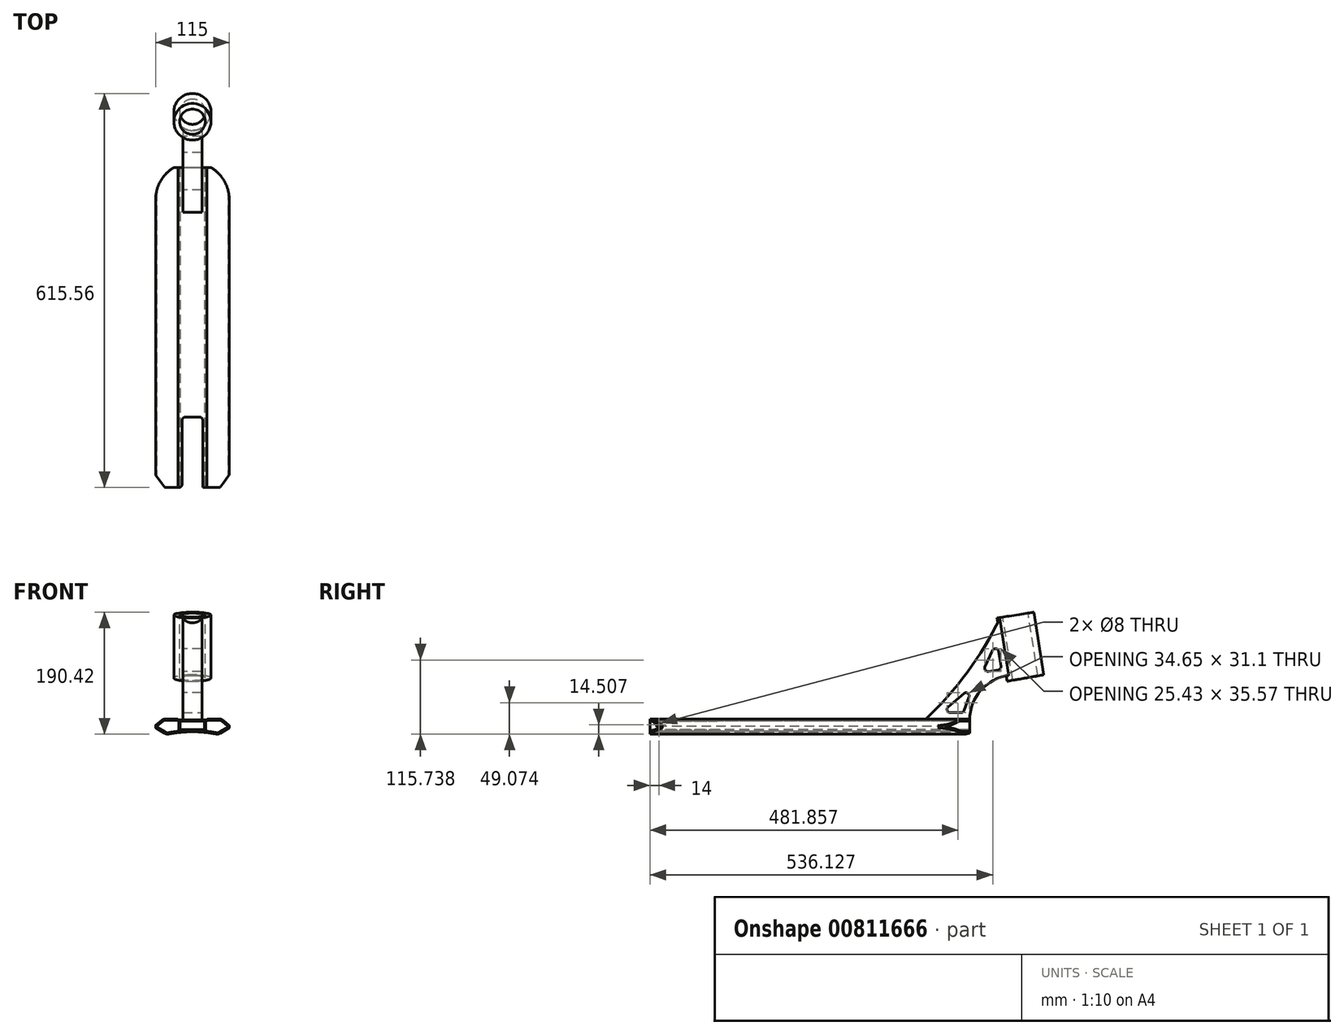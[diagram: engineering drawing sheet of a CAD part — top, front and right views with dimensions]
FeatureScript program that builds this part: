
annotation { "Feature Type Name" : "Feature", "Feature Type Description" : "" }
export const myFeature = defineFeature(function(context is Context, id is Id, definition is map)
    precondition{}
    {
        {
            var Q0;
            Q0=qCreatedBy(makeId("Front.planeOp"),FACE);
            var sketch = newSketch(context, id + "F0", { "sketchPlane" : qUnion([Q0])});
            skLineSegment(sketch, "E0", {"start": v(0, 46.76) * mm, "end": v(0, 0) * mm, "construction": true});
            skLineSegment(sketch, "E1", {"start": v(22.5, 13.36) * mm, "end": v(45.58, 13.36) * mm});
            skLineSegment(sketch, "E2", {"start": v(45.58, 13.36) * mm, "end": v(57.5, 3.36) * mm});
            skLineSegment(sketch, "E3", {"start": v(57.5, 3.36) * mm, "end": v(57.5, -0.64) * mm});
            skLineSegment(sketch, "E4", {"start": v(57.5, -0.64) * mm, "end": v(40.18, -10.64) * mm});
            skLineSegment(sketch, "E5.MirrorCS", {"start": v(-22.5, 13.36) * mm, "end": v(-45.58, 13.36) * mm});
            skLineSegment(sketch, "E6.MirrorCS", {"start": v(-45.58, 13.36) * mm, "end": v(-57.5, 3.36) * mm});
            skLineSegment(sketch, "E7.MirrorCS", {"start": v(-57.5, -0.64) * mm, "end": v(-40.18, -10.64) * mm});
            skLineSegment(sketch, "E8.MirrorCS", {"start": v(-57.5, 3.36) * mm, "end": v(-57.5, -0.64) * mm});
            skArc(sketch, "E9", {"start": v(40.18, -10.64) * mm, "mid": v(0, -6.56) * mm, "end": v(-40.18, -10.64) * mm});
            skLineSegment(sketch, "E10", {"start": v(-22.5, 13.36) * mm, "end": v(-22.5, 12.06) * mm});
            skLineSegment(sketch, "E11", {"start": v(-22.5, 12.06) * mm, "end": v(22.5, 12.06) * mm});
            skLineSegment(sketch, "E12", {"start": v(22.5, 12.06) * mm, "end": v(22.5, 13.36) * mm});
            skSolve(sketch);
        }
        {
            var Q0;
            Q0 = qSketchRegion(id + "F0", true);
            extrude(context, id + "F1", {"entities" : qUnion([Q0]), "endBound" : BoundingType.SYMMETRIC, "depth" : 500 * mm, "offsetDistance" : 25 * mm});
        }
        {
            var Q0;
            Q0=qCreatedBy(makeId("Front.planeOp"),FACE);
            var sketch = newSketch(context, id + "F2", { "sketchPlane" : qUnion([Q0])});
            skLineSegment(sketch, "E13.bottom", {"start": v(-19, 10.06) * mm, "end": v(19, 10.06) * mm});
            skLineSegment(sketch, "E13.top", {"start": v(-19, -2.94) * mm, "end": v(19, -2.94) * mm});
            skLineSegment(sketch, "E13.left", {"start": v(-19, 10.06) * mm, "end": v(-19, -2.94) * mm});
            skLineSegment(sketch, "E13.right", {"start": v(19, 10.06) * mm, "end": v(19, -2.94) * mm});
            skSolve(sketch);
        }
        {
            var Q0;
            Q0 = qSketchRegion(id + "F2", true);
            extrude(context, id + "F3", {"entities" : qUnion([Q0]), "operationType" : NewBodyOperationType.REMOVE, "endBound" : BoundingType.SYMMETRIC, "oppositeDirection" : true, "depth" : 500 * mm, "offsetDistance" : 25 * mm});
        }
        {
            var Q0;
            Q0=makeQuery(id+"F1.opExtrude","SWEPT_EDGE",EDGE,{"disambiguationData":[OSD([sQuery(id+"F0.wireOp",EDGE,"E1"),sQuery(id+"F0.wireOp",EDGE,"E12")])]});
            var Q1;
            Q1=makeQuery(id+"F1.opExtrude","SWEPT_EDGE",EDGE,{"disambiguationData":[OSD([sQuery(id+"F0.wireOp",EDGE,"E5.MirrorCS"),sQuery(id+"F0.wireOp",EDGE,"E10")])]});
            fillet(context, id + "F4", {"entities" : qUnion([Q0, Q1]), "radius" : 2 * mm, "tangentPropagation" : true, "allowEdgeOverflow" : false});
        }
        {
            var Q0;
            Q0=makeQuery(id+"F1.opExtrude","SWEPT_EDGE",EDGE,{"disambiguationData":[OSD([sQuery(id+"F0.wireOp",EDGE,"E5.MirrorCS"),sQuery(id+"F0.wireOp",EDGE,"E6.MirrorCS")])]});
            var Q1;
            Q1=makeQuery(id+"F1.opExtrude","SWEPT_EDGE",EDGE,{"disambiguationData":[OSD([sQuery(id+"F0.wireOp",EDGE,"E7.MirrorCS"),sQuery(id+"F0.wireOp",EDGE,"E9")])]});
            var Q2;
            Q2=makeQuery(id+"F1.opExtrude","SWEPT_EDGE",EDGE,{"disambiguationData":[OSD([sQuery(id+"F0.wireOp",EDGE,"E4"),sQuery(id+"F0.wireOp",EDGE,"E9")])]});
            var Q3;
            Q3=makeQuery(id+"F1.opExtrude","SWEPT_EDGE",EDGE,{"disambiguationData":[OSD([sQuery(id+"F0.wireOp",EDGE,"E1"),sQuery(id+"F0.wireOp",EDGE,"E2")])]});
            fillet(context, id + "F5", {"entities" : qUnion([Q0, Q1, Q2, Q3]), "radius" : 9 * mm, "tangentPropagation" : true, "allowEdgeOverflow" : false});
        }
        {
            var Q0;
            Q0=makeQuery(id+"F1.opExtrude","SWEPT_EDGE",EDGE,{"disambiguationData":[OSD([sQuery(id+"F0.wireOp",EDGE,"E2"),sQuery(id+"F0.wireOp",EDGE,"E3")])]});
            var Q1;
            Q1=makeQuery(id+"F1.opExtrude","SWEPT_EDGE",EDGE,{"disambiguationData":[OSD([sQuery(id+"F0.wireOp",EDGE,"E3"),sQuery(id+"F0.wireOp",EDGE,"E4")])]});
            var Q2;
            Q2=makeQuery(id+"F1.opExtrude","SWEPT_EDGE",EDGE,{"disambiguationData":[OSD([sQuery(id+"F0.wireOp",EDGE,"E7.MirrorCS"),sQuery(id+"F0.wireOp",EDGE,"E8.MirrorCS")])]});
            var Q3;
            Q3=makeQuery(id+"F1.opExtrude","SWEPT_EDGE",EDGE,{"disambiguationData":[OSD([sQuery(id+"F0.wireOp",EDGE,"E6.MirrorCS"),sQuery(id+"F0.wireOp",EDGE,"E8.MirrorCS")])]});
            fillet(context, id + "F6", {"entities" : qUnion([Q0, Q1, Q2, Q3]), "radius" : 1 * mm, "tangentPropagation" : true, "allowEdgeOverflow" : false});
        }
        {
            var Q0;
            Q0=makeQuery(id+"F1.opExtrude","CAP_FACE",FACE,{"disambiguationData":[OSD([sQuery(id+"F0.wireOp",EDGE,"E1"),sQuery(id+"F0.wireOp",EDGE,"E2"),sQuery(id+"F0.wireOp",EDGE,"E3"),sQuery(id+"F0.wireOp",EDGE,"E4"),sQuery(id+"F0.wireOp",EDGE,"E5.MirrorCS"),sQuery(id+"F0.wireOp",EDGE,"E6.MirrorCS"),sQuery(id+"F0.wireOp",EDGE,"E7.MirrorCS"),sQuery(id+"F0.wireOp",EDGE,"E8.MirrorCS"),sQuery(id+"F0.wireOp",EDGE,"E9"),sQuery(id+"F0.wireOp",EDGE,"E10"),sQuery(id+"F0.wireOp",EDGE,"E11"),sQuery(id+"F0.wireOp",EDGE,"E12")])],"isStart":false});
            var sketch = newSketch(context, id + "F7", { "sketchPlane" : qUnion([Q0])});
            skLineSegment(sketch, "E14.0.0", {"start": v(-48.1, 11.26) * mm, "end": v(-57.14, 3.66) * mm});
            skArc(sketch, "E14.0.1", {"start": v(-57.14, 3.66) * mm, "mid": v(-57.4, 3.32) * mm, "end": v(-57.5, 2.9) * mm});
            skLineSegment(sketch, "E14.0.2", {"start": v(-57.5, 2.9) * mm, "end": v(-57.5, -0.06) * mm});
            skArc(sketch, "E14.0.3", {"start": v(-57.5, -0.06) * mm, "mid": v(-57.37, -0.56) * mm, "end": v(-57, -0.92) * mm});
            skLineSegment(sketch, "E14.0.4", {"start": v(-57, -0.92) * mm, "end": v(-43.1, -8.95) * mm});
            skArc(sketch, "E14.0.5", {"start": v(-43.1, -8.95) * mm, "mid": v(-40.12, -10.03) * mm, "end": v(-36.94, -10) * mm});
            skArc(sketch, "E14.0.6", {"start": v(-36.94, -10) * mm, "mid": v(0, -6.56) * mm, "end": v(36.94, -10) * mm});
            skArc(sketch, "E14.0.7", {"start": v(36.94, -10) * mm, "mid": v(40.12, -10.03) * mm, "end": v(43.1, -8.95) * mm});
            skLineSegment(sketch, "E14.0.8", {"start": v(43.1, -8.95) * mm, "end": v(57, -0.92) * mm});
            skArc(sketch, "E14.0.9", {"start": v(57, -0.92) * mm, "mid": v(57.37, -0.56) * mm, "end": v(57.5, -0.06) * mm});
            skLineSegment(sketch, "E14.0.10", {"start": v(57.5, -0.06) * mm, "end": v(57.5, 2.9) * mm});
            skArc(sketch, "E14.0.11", {"start": v(57.5, 2.9) * mm, "mid": v(57.4, 3.32) * mm, "end": v(57.14, 3.66) * mm});
            skLineSegment(sketch, "E14.0.12", {"start": v(57.14, 3.66) * mm, "end": v(48.1, 11.26) * mm});
            skArc(sketch, "E14.0.13", {"start": v(48.1, 11.26) * mm, "mid": v(45.38, 12.82) * mm, "end": v(42.3, 13.36) * mm});
            skLineSegment(sketch, "E14.0.14", {"start": v(42.3, 13.36) * mm, "end": v(24.37, 13.36) * mm});
            skArc(sketch, "E14.0.15", {"start": v(24.37, 13.36) * mm, "mid": v(23.23, 13) * mm, "end": v(22.5, 12.06) * mm});
            skLineSegment(sketch, "E14.0.16", {"start": v(22.5, 12.06) * mm, "end": v(-22.5, 12.06) * mm});
            skArc(sketch, "E14.0.17", {"start": v(-22.5, 12.06) * mm, "mid": v(-23.23, 13) * mm, "end": v(-24.37, 13.36) * mm});
            skLineSegment(sketch, "E14.0.18", {"start": v(-24.37, 13.36) * mm, "end": v(-42.3, 13.36) * mm});
            skArc(sketch, "E14.0.19", {"start": v(-42.3, 13.36) * mm, "mid": v(-45.38, 12.82) * mm, "end": v(-48.1, 11.26) * mm});
            skArc(sketch, "E15.0", {"start": v(-37.3, -8.03) * mm, "mid": v(0, -4.56) * mm, "end": v(37.3, -8.03) * mm});
            skArc(sketch, "E15.1", {"start": v(-42.1, -7.22) * mm, "mid": v(-39.78, -8.05) * mm, "end": v(-37.3, -8.03) * mm});
            skLineSegment(sketch, "E15.2", {"start": v(-55.62, 0.59) * mm, "end": v(-42.1, -7.22) * mm});
            skLineSegment(sketch, "E15.6", {"start": v(-24.37, 11.36) * mm, "end": v(-24.37, 11.36) * mm});
            skLineSegment(sketch, "E15.7", {"start": v(-24.37, 11.36) * mm, "end": v(-42.3, 11.36) * mm});
            skArc(sketch, "E15.8", {"start": v(-42.3, 11.36) * mm, "mid": v(-44.7, 10.94) * mm, "end": v(-46.8, 9.73) * mm});
            skLineSegment(sketch, "E15.9", {"start": v(-46.8, 9.73) * mm, "end": v(-55.86, 2.13) * mm});
            skArc(sketch, "E16", {"start": v(-55.86, 2.13) * mm, "mid": v(-56.1, 1.3) * mm, "end": v(-55.62, 0.59) * mm});
            skArc(sketch, "E17", {"start": v(-22.5, 10.06) * mm, "mid": v(-23.23, 11) * mm, "end": v(-24.37, 11.36) * mm});
            skLineSegment(sketch, "E18", {"start": v(-22.5, 10.06) * mm, "end": v(-21, 10.06) * mm});
            skLineSegment(sketch, "E19", {"start": v(-21, 10.06) * mm, "end": v(-21, -5.65) * mm});
            skLineSegment(sketch, "E20", {"start": v(0, 12.06) * mm, "end": v(0, 30.3) * mm, "construction": true});
            skLineSegment(sketch, "E21.MirrorCS", {"start": v(24.37, 11.36) * mm, "end": v(42.3, 11.36) * mm});
            skArc(sketch, "E22.MirrorCS", {"start": v(42.3, 11.36) * mm, "mid": v(44.7, 10.94) * mm, "end": v(46.8, 9.73) * mm});
            skLineSegment(sketch, "E23.MirrorCS", {"start": v(46.8, 9.73) * mm, "end": v(55.86, 2.13) * mm});
            skArc(sketch, "E24.MirrorCS", {"start": v(55.86, 2.13) * mm, "mid": v(56.1, 1.3) * mm, "end": v(55.62, 0.59) * mm});
            skLineSegment(sketch, "E25.MirrorCS", {"start": v(55.62, 0.59) * mm, "end": v(42.1, -7.22) * mm});
            skArc(sketch, "E26.MirrorCS", {"start": v(42.1, -7.22) * mm, "mid": v(39.78, -8.05) * mm, "end": v(37.3, -8.03) * mm});
            skArc(sketch, "E27.MirrorCS", {"start": v(37.3, -8.03) * mm, "mid": v(0, -4.56) * mm, "end": v(-37.3, -8.03) * mm});
            skLineSegment(sketch, "E28.MirrorCS", {"start": v(21, 10.06) * mm, "end": v(21, -5.65) * mm});
            skLineSegment(sketch, "E29.MirrorCS", {"start": v(22.5, 10.06) * mm, "end": v(21, 10.06) * mm});
            skArc(sketch, "E30.MirrorCS", {"start": v(22.5, 10.06) * mm, "mid": v(23.23, 11) * mm, "end": v(24.37, 11.36) * mm});
            skSolve(sketch);
        }
        {
            var Q0;
            Q0=makeQuery(id+"F7.imprint","IMPRINT",FACE,{"disambiguationData":[TD([[makeQuery(id+"F7.imprint","IMPRINT",EDGE,{"derivedFrom":makeQuery(id+"F3.boolean.opBoolean","COPY",EDGE,{"derivedFrom":makeQuery(id+"F3.opExtrude","CAP_EDGE",EDGE,{"disambiguationData":[OSD([sQuery(id+"F2.wireOp",EDGE,"E13.bottom")])],"isStart":true})})}),-1.0]])]});
            var Q1;
            {var subQ0=sQuery(id+"F7.wireOp",EDGE,"E15.1");Q1=makeQuery(id+"F7.imprint","IMPRINT",FACE,{"disambiguationData":[TD([[makeQuery(id+"F7.imprint","IMPRINT",EDGE,{"derivedFrom":subQ0}),1.0]])]});}
            var Q2;
            Q2=makeQuery(id+"F7.imprint","IMPRINT",FACE,{"disambiguationData":[TD([[makeQuery(id+"F7.imprint","IMPRINT",EDGE,{"derivedFrom":sQuery(id+"F7.wireOp",EDGE,"E21.MirrorCS")}),-1.0]])]});
            extrude(context, id + "F8", {"entities" : qUnion([Q0, Q1, Q2]), "operationType" : NewBodyOperationType.REMOVE, "endBound" : BoundingType.THROUGH_ALL, "oppositeDirection" : true, "depth" : 25 * mm, "offsetDistance" : 25 * mm});
        }
        {
            var Q0;
            Q0=qCreatedBy(makeId("Top.planeOp"),FACE);
            var sketch = newSketch(context, id + "F9", { "sketchPlane" : qUnion([Q0])});
            skArc(sketch, "E31", {"start": v(57.5, 200) * mm, "mid": v(0, 257.5) * mm, "end": v(-57.5, 200) * mm});
            skLineSegment(sketch, "E32", {"start": v(-57.5, 200) * mm, "end": v(-57.5, 280) * mm});
            skLineSegment(sketch, "E33", {"start": v(57.5, 200) * mm, "end": v(57.5, 280) * mm});
            skLineSegment(sketch, "E34", {"start": v(57.5, 280) * mm, "end": v(-57.5, 280) * mm});
            skSolve(sketch);
        }
        {
            var Q0;
            Q0 = qSketchRegion(id + "F9", true);
            extrude(context, id + "F10", {"entities" : qUnion([Q0]), "operationType" : NewBodyOperationType.REMOVE, "endBound" : BoundingType.THROUGH_ALL, "oppositeDirection" : true, "depth" : 25 * mm, "offsetDistance" : 25 * mm, "hasSecondDirection" : true, "secondDirectionBound" : SecondDirectionBoundingType.THROUGH_ALL, "secondDirectionOppositeDirection" : false, "secondDirectionDepth" : 25 * mm});
        }
        {
            var Q0;
            Q0=qCreatedBy(makeId("Top.planeOp"),FACE);
            var sketch = newSketch(context, id + "F11", { "sketchPlane" : qUnion([Q0])});
            skLineSegment(sketch, "E35", {"start": v(-16, -140) * mm, "end": v(16, -140) * mm});
            skLineSegment(sketch, "E36", {"start": v(16, -140) * mm, "end": v(16, -250) * mm});
            skLineSegment(sketch, "E37", {"start": v(-16, -140) * mm, "end": v(-16, -250) * mm});
            skLineSegment(sketch, "E38", {"start": v(-16, -250) * mm, "end": v(-43.3, -250) * mm});
            skLineSegment(sketch, "E39", {"start": v(-43.3, -250) * mm, "end": v(-68, -216) * mm});
            skLineSegment(sketch, "E40", {"start": v(-68, -216) * mm, "end": v(-68, -346) * mm});
            skLineSegment(sketch, "E41", {"start": v(16, -250) * mm, "end": v(43.3, -250) * mm});
            skLineSegment(sketch, "E42", {"start": v(43.3, -250) * mm, "end": v(68, -216) * mm});
            skLineSegment(sketch, "E43", {"start": v(68, -216) * mm, "end": v(68, -346) * mm});
            skLineSegment(sketch, "E44", {"start": v(68, -346) * mm, "end": v(-68, -346) * mm});
            skSolve(sketch);
        }
        {
            var Q0;
            Q0 = qSketchRegion(id + "F11", true);
            extrude(context, id + "F12", {"entities" : qUnion([Q0]), "operationType" : NewBodyOperationType.REMOVE, "endBound" : BoundingType.THROUGH_ALL, "oppositeDirection" : true, "depth" : 25 * mm, "offsetDistance" : 25 * mm, "hasSecondDirection" : true, "secondDirectionBound" : SecondDirectionBoundingType.THROUGH_ALL, "secondDirectionOppositeDirection" : false, "secondDirectionDepth" : 25 * mm});
        }
        {
            var Q0;
            {var subQ0=sQuery(id+"F0.wireOp",EDGE,"E9");var subQ1=sQuery(id+"F11.wireOp",EDGE,"E36");Q0=makeQuery(id+"F12.boolean.opBoolean","COPY",EDGE,{"disambiguationData":[TD([makeQuery(id+"F1.opExtrude","SWEPT_FACE",FACE,{"disambiguationData":[OSD([subQ0])]})])],"derivedFrom":makeQuery(id+"F12.opExtrude","SWEPT_EDGE",EDGE,{"disambiguationData":[OSD([subQ1,sQuery(id+"F11.wireOp",EDGE,"E41")])]})});}
            var Q1;
            {var subQ0=sQuery(id+"F0.wireOp",EDGE,"E9");var subQ1=sQuery(id+"F11.wireOp",EDGE,"E37");Q1=makeQuery(id+"F12.boolean.opBoolean","COPY",EDGE,{"disambiguationData":[TD([makeQuery(id+"F1.opExtrude","SWEPT_FACE",FACE,{"disambiguationData":[OSD([subQ0])]})])],"derivedFrom":makeQuery(id+"F12.opExtrude","SWEPT_EDGE",EDGE,{"disambiguationData":[OSD([subQ1,sQuery(id+"F11.wireOp",EDGE,"E38")])]})});}
            var Q2;
            {var subQ0=sQuery(id+"F11.wireOp",EDGE,"E35");var subQ1=sQuery(id+"F11.wireOp",EDGE,"E37");Q2=makeQuery(id+"F12.boolean.opBoolean","COPY",EDGE,{"disambiguationData":[TD([makeQuery(id+"F1.opExtrude","SWEPT_FACE",FACE,{"disambiguationData":[OSD([sQuery(id+"F0.wireOp",EDGE,"E11")])]})])],"derivedFrom":makeQuery(id+"F12.opExtrude","SWEPT_EDGE",EDGE,{"disambiguationData":[OSD([subQ0,subQ1])]})});}
            var Q3;
            {var subQ0=sQuery(id+"F11.wireOp",EDGE,"E36");var subQ1=sQuery(id+"F11.wireOp",EDGE,"E35");Q3=makeQuery(id+"F12.boolean.opBoolean","COPY",EDGE,{"disambiguationData":[TD([makeQuery(id+"F1.opExtrude","SWEPT_FACE",FACE,{"disambiguationData":[OSD([sQuery(id+"F0.wireOp",EDGE,"E11")])]})])],"derivedFrom":makeQuery(id+"F12.opExtrude","SWEPT_EDGE",EDGE,{"disambiguationData":[OSD([subQ1,subQ0])]})});}
            var Q4;
            {var subQ0=sQuery(id+"F11.wireOp",EDGE,"E35");var subQ1=sQuery(id+"F11.wireOp",EDGE,"E37");Q4=makeQuery(id+"F12.boolean.opBoolean","COPY",EDGE,{"disambiguationData":[TD([makeQuery(id+"F1.opExtrude","SWEPT_FACE",FACE,{"disambiguationData":[OSD([sQuery(id+"F0.wireOp",EDGE,"E9")])]})])],"derivedFrom":makeQuery(id+"F12.opExtrude","SWEPT_EDGE",EDGE,{"disambiguationData":[OSD([subQ0,subQ1])]})});}
            var Q5;
            {var subQ0=sQuery(id+"F11.wireOp",EDGE,"E35");var subQ1=sQuery(id+"F11.wireOp",EDGE,"E36");Q5=makeQuery(id+"F12.boolean.opBoolean","COPY",EDGE,{"disambiguationData":[TD([makeQuery(id+"F1.opExtrude","SWEPT_FACE",FACE,{"disambiguationData":[OSD([sQuery(id+"F0.wireOp",EDGE,"E9")])]})])],"derivedFrom":makeQuery(id+"F12.opExtrude","SWEPT_EDGE",EDGE,{"disambiguationData":[OSD([subQ0,subQ1])]})});}
            fillet(context, id + "F13", {"entities" : qUnion([Q0, Q1, Q2, Q3, Q4, Q5]), "radius" : 5 * mm, "tangentPropagation" : true, "allowEdgeOverflow" : false});
        }
        {
            var Q0;
            Q0=qCreatedBy(makeId("Right.planeOp"),FACE);
            var sketch = newSketch(context, id + "F14", { "sketchPlane" : qUnion([Q0])});
            skArc(sketch, "E45", {"start": v(180.01, 12.03) * mm, "mid": v(246.36, 86.65) * mm, "end": v(298.13, 172.03) * mm});
            skLineSegment(sketch, "E46", {"start": v(250.01, 12.03) * mm, "end": v(180.01, 12.03) * mm});
            skArc(sketch, "E47", {"start": v(314.6, 81.83) * mm, "mid": v(268.64, 59.58) * mm, "end": v(250.01, 12.03) * mm});
            skLineSegment(sketch, "E48", {"start": v(314.6, 81.83) * mm, "end": v(316.05, 73.65) * mm});
            skLineSegment(sketch, "E49", {"start": v(316.05, 73.65) * mm, "end": v(361.35, 81.64) * mm});
            skLineSegment(sketch, "E50", {"start": v(361.35, 81.64) * mm, "end": v(344.13, 179.32) * mm});
            skLineSegment(sketch, "E51", {"start": v(344.13, 179.32) * mm, "end": v(298.13, 172.03) * mm});
            skSolve(sketch);
        }
        {
            var Q0;
            Q0 = qSketchRegion(id + "F14", true);
            extrude(context, id + "F15", {"entities" : qUnion([Q0]), "operationType" : NewBodyOperationType.ADD, "endBound" : BoundingType.SYMMETRIC, "depth" : 30 * mm, "offsetDistance" : 25 * mm});
        }
        {
            var Q0;
            Q0=makeQuery(id+"F15.opExtrude","SWEPT_FACE",FACE,{"disambiguationData":[OSD([sQuery(id+"F14.wireOp",EDGE,"E51")])]});
            var sketch = newSketch(context, id + "F16", { "sketchPlane" : qUnion([Q0])});
            skPoint(sketch, "E52.centerSnap0", {"position": v(-15, 344.66) * mm});
            skCircle(sketch, "E53", {"center": v(0, 344.94) * mm, "radius": 29 * mm});
            skPoint(sketch, "E53.centerSnap0", {"position": v(0, 321.37) * mm});
            skSolve(sketch);
        }
        {
            var Q0;
            Q0 = qSketchRegion(id + "F16", true);
            var Q1;
            Q1=makeQuery(id+"F15.opExtrude","SWEPT_FACE",FACE,{"disambiguationData":[OSD([sQuery(id+"F14.wireOp",EDGE,"E49")])]});
            extrude(context, id + "F17", {"entities" : qUnion([Q0]), "operationType" : NewBodyOperationType.ADD, "endBound" : BoundingType.UP_TO_SURFACE, "oppositeDirection" : true, "depth" : 25 * mm, "endBoundEntityFace" : qUnion([Q1]), "offsetDistance" : 25 * mm});
        }
        {
            var Q0;
            Q0=makeQuery(id+"F17.boolean.opBoolean","MERGE",FACE,{"derivedFrom":[makeQuery(id+"F15.opExtrude","SWEPT_FACE",FACE,{"disambiguationData":[OSD([sQuery(id+"F14.wireOp",EDGE,"E51")])]}),makeQuery(id+"F17.opExtrude","CAP_FACE",FACE,{"disambiguationData":[OSD([sQuery(id+"F16.wireOp",EDGE,"E53")])],"isStart":true})]});
            var sketch = newSketch(context, id + "F18", { "sketchPlane" : qUnion([Q0])});
            skPoint(sketch, "E54", {"position": v(0, 344.94) * mm});
            skSolve(sketch);
        }
        {
            var Q0;
            Q0=sQuery(id+"F18.wireOp",VERTEX,"E54");
            var Q1;
            Q1=makeQuery(id+"F1.opExtrude","SWEPT_BODY",BODY,{"disambiguationData":[OSD([sQuery(id+"F0.wireOp",EDGE,"E1"),sQuery(id+"F0.wireOp",EDGE,"E2"),sQuery(id+"F0.wireOp",EDGE,"E3"),sQuery(id+"F0.wireOp",EDGE,"E4"),sQuery(id+"F0.wireOp",EDGE,"E5.MirrorCS"),sQuery(id+"F0.wireOp",EDGE,"E6.MirrorCS"),sQuery(id+"F0.wireOp",EDGE,"E7.MirrorCS"),sQuery(id+"F0.wireOp",EDGE,"E8.MirrorCS"),sQuery(id+"F0.wireOp",EDGE,"E9"),sQuery(id+"F0.wireOp",EDGE,"E10"),sQuery(id+"F0.wireOp",EDGE,"E11"),sQuery(id+"F0.wireOp",EDGE,"E12")])]});
            hole(context, id + "F19", {"style" : HoleStyle.SIMPLE, "endStyle" : HoleEndStyle.THROUGH, "holeDiameter" : 40 * mm, "majorDiameter" : 5 * mm, "isTappedThrough" : true, "tappedDepth" : 12 * mm, "tapClearance" : 3, "locations" : qUnion([Q0]), "scope" : qUnion([Q1])});
        }
        {
            var Q0;
            Q0=makeQuery(id+"F8.boolean.opBoolean","COPY",FACE,{"derivedFrom":makeQuery(id+"F8.opExtrude","SWEPT_FACE",FACE,{"disambiguationData":[OSD([sQuery(id+"F7.wireOp",EDGE,"E28.MirrorCS")])]})});
            var sketch = newSketch(context, id + "F20", { "sketchPlane" : qUnion([Q0])});
            skPoint(sketch, "E55", {"position": v(-236, 4.35) * mm});
            skSolve(sketch);
        }
        {
            var Q0;
            Q0=sQuery(id+"F20.wireOp",VERTEX,"E55");
            var Q1;
            Q1=makeQuery(id+"F1.opExtrude","SWEPT_BODY",BODY,{"disambiguationData":[OSD([sQuery(id+"F0.wireOp",EDGE,"E1"),sQuery(id+"F0.wireOp",EDGE,"E2"),sQuery(id+"F0.wireOp",EDGE,"E3"),sQuery(id+"F0.wireOp",EDGE,"E4"),sQuery(id+"F0.wireOp",EDGE,"E5.MirrorCS"),sQuery(id+"F0.wireOp",EDGE,"E6.MirrorCS"),sQuery(id+"F0.wireOp",EDGE,"E7.MirrorCS"),sQuery(id+"F0.wireOp",EDGE,"E8.MirrorCS"),sQuery(id+"F0.wireOp",EDGE,"E9"),sQuery(id+"F0.wireOp",EDGE,"E10"),sQuery(id+"F0.wireOp",EDGE,"E11"),sQuery(id+"F0.wireOp",EDGE,"E12")])]});
            hole(context, id + "F21", {"style" : HoleStyle.SIMPLE, "endStyle" : HoleEndStyle.BLIND, "holeDiameter" : 8 * mm, "majorDiameter" : 5 * mm, "holeDepth" : 50 * mm, "isTappedThrough" : true, "tappedDepth" : 12 * mm, "tapClearance" : 3, "locations" : qUnion([Q0]), "scope" : qUnion([Q1])});
        }
        {
            var Q0;
            Q0=makeQuery(id+"F15.opExtrude","CAP_FACE",FACE,{"disambiguationData":[OSD([sQuery(id+"F14.wireOp",EDGE,"E45"),sQuery(id+"F14.wireOp",EDGE,"E46"),sQuery(id+"F14.wireOp",EDGE,"E47"),sQuery(id+"F14.wireOp",EDGE,"E48"),sQuery(id+"F14.wireOp",EDGE,"E49"),sQuery(id+"F14.wireOp",EDGE,"E50"),sQuery(id+"F14.wireOp",EDGE,"E51")])],"isStart":false});
            var sketch = newSketch(context, id + "F22", { "sketchPlane" : qUnion([Q0])});
            skLineSegment(sketch, "E56", {"start": v(292.53, 135.5) * mm, "end": v(299.57, 91.06) * mm});
            skLineSegment(sketch, "E57", {"start": v(299.57, 91.06) * mm, "end": v(269.94, 86.36) * mm});
            skLineSegment(sketch, "E58", {"start": v(269.94, 86.36) * mm, "end": v(292.53, 135.5) * mm});
            skLineSegment(sketch, "E59", {"start": v(255.4, 65.65) * mm, "end": v(240, 23.36) * mm});
            skLineSegment(sketch, "E60", {"start": v(240, 23.36) * mm, "end": v(206, 23.36) * mm});
            skLineSegment(sketch, "E61", {"start": v(206, 23.36) * mm, "end": v(255.4, 65.65) * mm});
            skSolve(sketch);
        }
        {
            var Q0;
            Q0 = qSketchRegion(id + "F22", true);
            extrude(context, id + "F23", {"entities" : qUnion([Q0]), "operationType" : NewBodyOperationType.REMOVE, "endBound" : BoundingType.THROUGH_ALL, "oppositeDirection" : true, "depth" : 25 * mm, "offsetDistance" : 25 * mm});
        }
        {
            var Q0;
            Q0=makeQuery(id+"F23.boolean.opBoolean","COPY",EDGE,{"derivedFrom":makeQuery(id+"F23.opExtrude","SWEPT_EDGE",EDGE,{"disambiguationData":[OSD([sQuery(id+"F22.wireOp",EDGE,"E57"),sQuery(id+"F22.wireOp",EDGE,"E58")])]})});
            var Q1;
            Q1=makeQuery(id+"F23.boolean.opBoolean","COPY",EDGE,{"derivedFrom":makeQuery(id+"F23.opExtrude","SWEPT_EDGE",EDGE,{"disambiguationData":[OSD([sQuery(id+"F22.wireOp",EDGE,"E56"),sQuery(id+"F22.wireOp",EDGE,"E58")])]})});
            var Q2;
            Q2=makeQuery(id+"F23.boolean.opBoolean","COPY",EDGE,{"derivedFrom":makeQuery(id+"F23.opExtrude","SWEPT_EDGE",EDGE,{"disambiguationData":[OSD([sQuery(id+"F22.wireOp",EDGE,"E56"),sQuery(id+"F22.wireOp",EDGE,"E57")])]})});
            var Q3;
            Q3=makeQuery(id+"F23.boolean.opBoolean","COPY",EDGE,{"derivedFrom":makeQuery(id+"F23.opExtrude","SWEPT_EDGE",EDGE,{"disambiguationData":[OSD([sQuery(id+"F22.wireOp",EDGE,"E60"),sQuery(id+"F22.wireOp",EDGE,"E61")])]})});
            var Q4;
            Q4=makeQuery(id+"F23.boolean.opBoolean","COPY",EDGE,{"derivedFrom":makeQuery(id+"F23.opExtrude","SWEPT_EDGE",EDGE,{"disambiguationData":[OSD([sQuery(id+"F22.wireOp",EDGE,"E59"),sQuery(id+"F22.wireOp",EDGE,"E61")])]})});
            var Q5;
            Q5=makeQuery(id+"F23.boolean.opBoolean","COPY",EDGE,{"derivedFrom":makeQuery(id+"F23.opExtrude","SWEPT_EDGE",EDGE,{"disambiguationData":[OSD([sQuery(id+"F22.wireOp",EDGE,"E59"),sQuery(id+"F22.wireOp",EDGE,"E60")])]})});
            fillet(context, id + "F24", {"entities" : qUnion([Q0, Q1, Q2, Q3, Q4, Q5]), "radius" : 5 * mm, "tangentPropagation" : true, "allowEdgeOverflow" : false});
        }
    });
